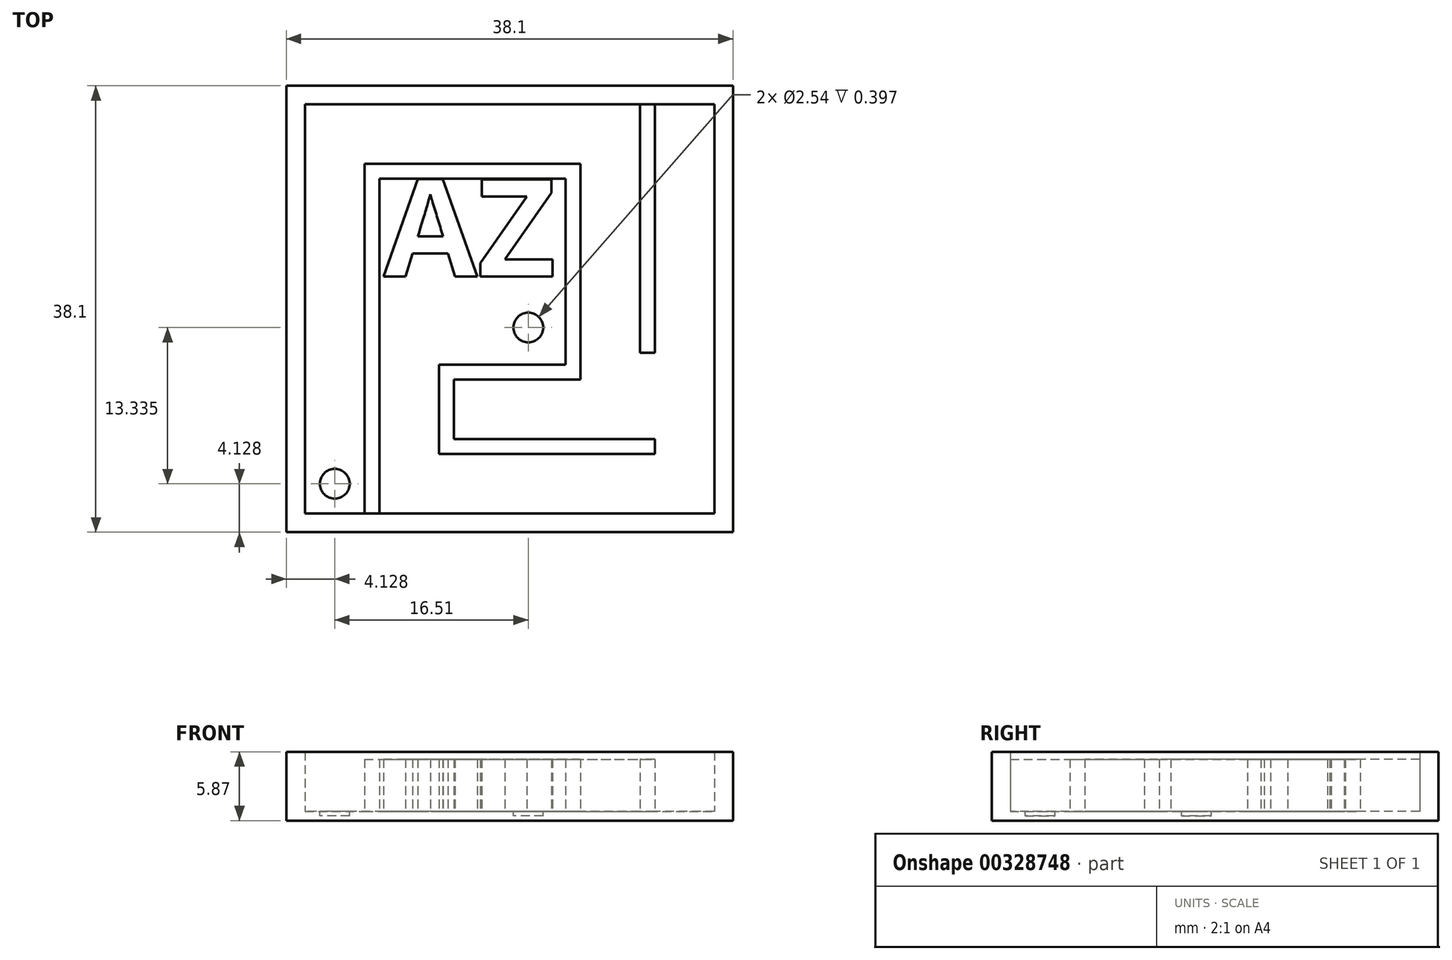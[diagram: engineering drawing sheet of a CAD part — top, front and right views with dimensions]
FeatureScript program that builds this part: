
annotation { "Feature Type Name" : "Feature", "Feature Type Description" : "" }
export const myFeature = defineFeature(function(context is Context, id is Id, definition is map)
    precondition{}
    {
        {
            var Q0;
            Q0=qCreatedBy(makeId("Top.planeOp"),FACE);
            var sketch = newSketch(context, id + "F0", { "sketchPlane" : qUnion([Q0])});
            skLineSegment(sketch, "E0.bottom", {"start": v(19.05, 19.05) * mm, "end": v(-19.05, 19.05) * mm});
            skLineSegment(sketch, "E0.top", {"start": v(19.05, -19.05) * mm, "end": v(-19.05, -19.05) * mm});
            skLineSegment(sketch, "E0.left", {"start": v(19.05, 19.05) * mm, "end": v(19.05, -19.05) * mm});
            skLineSegment(sketch, "E0.right", {"start": v(-19.05, 19.05) * mm, "end": v(-19.05, -19.05) * mm});
            skSolve(sketch);
        }
        {
            var Q0;
            Q0 = qSketchRegion(id + "F0", true);
            extrude(context, id + "F1", {"entities" : qUnion([Q0]), "depth" : 0.8 * mm});
        }
        {
            var Q0;
            Q0=makeQuery(id+"F1.opExtrude","CAP_FACE",FACE,{"disambiguationData":[OSD([sQuery(id+"F0.wireOp",EDGE,"E0.bottom"),sQuery(id+"F0.wireOp",EDGE,"E0.top"),sQuery(id+"F0.wireOp",EDGE,"E0.left"),sQuery(id+"F0.wireOp",EDGE,"E0.right")])],"isStart":false});
            var sketch = newSketch(context, id + "F2", { "sketchPlane" : qUnion([Q0])});
            skLineSegment(sketch, "E1.0", {"start": v(-17.46, -17.46) * mm, "end": v(17.46, -17.46) * mm});
            skLineSegment(sketch, "E1.1", {"start": v(-17.46, 17.46) * mm, "end": v(-17.46, -17.46) * mm});
            skLineSegment(sketch, "E1.2", {"start": v(17.46, 17.46) * mm, "end": v(-17.46, 17.46) * mm});
            skLineSegment(sketch, "E1.3", {"start": v(17.46, -17.46) * mm, "end": v(17.46, 17.46) * mm});
            skSolve(sketch);
        }
        {
            var Q0;
            Q0=makeQuery(id+"F2.imprint","IMPRINT",FACE,{"disambiguationData":[TD([[makeQuery(id+"F2.imprint","IMPRINT",EDGE,{"derivedFrom":sQuery(id+"F2.wireOp",EDGE,"E1.0")}),-1.0]])]});
            extrude(context, id + "F3", {"entities" : qUnion([Q0]), "operationType" : NewBodyOperationType.ADD, "depth" : 5.08 * mm});
        }
        {
            var Q0;
            Q0=makeQuery(id+"F1.opExtrude","CAP_FACE",FACE,{"disambiguationData":[OSD([sQuery(id+"F0.wireOp",EDGE,"E0.bottom"),sQuery(id+"F0.wireOp",EDGE,"E0.top"),sQuery(id+"F0.wireOp",EDGE,"E0.left"),sQuery(id+"F0.wireOp",EDGE,"E0.right")])],"isStart":false});
            var sketch = newSketch(context, id + "F4", { "sketchPlane" : qUnion([Q0])});
            skLineSegment(sketch, "E2.bottom", {"start": v(-12.38, -17.46) * mm, "end": v(-11.11, -17.46) * mm});
            skLineSegment(sketch, "E2.top", {"start": v(-12.38, 12.38) * mm, "end": v(-11.11, 12.38) * mm});
            skLineSegment(sketch, "E2.left", {"start": v(-12.38, -17.46) * mm, "end": v(-12.38, 12.38) * mm});
            skLineSegment(sketch, "E2.right", {"start": v(-11.11, -17.46) * mm, "end": v(-11.11, 11.11) * mm});
            skLineSegment(sketch, "E3.bottom", {"start": v(-11.11, 12.38) * mm, "end": v(6.03, 12.38) * mm});
            skLineSegment(sketch, "E3.top", {"start": v(-11.11, 11.11) * mm, "end": v(4.76, 11.11) * mm});
            skLineSegment(sketch, "E3.right", {"start": v(6.03, 12.38) * mm, "end": v(6.03, 11.11) * mm});
            skLineSegment(sketch, "E4.bottom", {"start": v(12.38, 17.46) * mm, "end": v(11.11, 17.46) * mm});
            skLineSegment(sketch, "E4.top", {"start": v(12.38, -3.75) * mm, "end": v(11.11, -3.75) * mm});
            skLineSegment(sketch, "E4.left", {"start": v(12.38, 17.46) * mm, "end": v(12.38, -3.75) * mm});
            skLineSegment(sketch, "E4.right", {"start": v(11.11, 17.46) * mm, "end": v(11.11, -3.75) * mm});
            skLineSegment(sketch, "E5.top", {"start": v(6.03, -6.03) * mm, "end": v(4.76, -6.03) * mm});
            skLineSegment(sketch, "E5.left", {"start": v(6.03, 11.11) * mm, "end": v(6.03, -6.03) * mm});
            skLineSegment(sketch, "E5.right", {"start": v(4.76, 11.11) * mm, "end": v(4.76, -4.76) * mm});
            skLineSegment(sketch, "E6.bottom", {"start": v(4.76, -6.03) * mm, "end": v(-4.76, -6.03) * mm});
            skLineSegment(sketch, "E6.top", {"start": v(4.76, -4.76) * mm, "end": v(-4.76, -4.76) * mm});
            skLineSegment(sketch, "E6.right", {"start": v(-6.03, -6.03) * mm, "end": v(-6.03, -4.76) * mm});
            skLineSegment(sketch, "E7.top", {"start": v(-6.03, -12.38) * mm, "end": v(-4.76, -12.38) * mm});
            skLineSegment(sketch, "E7.left", {"start": v(-6.03, -6.03) * mm, "end": v(-6.03, -12.38) * mm});
            skLineSegment(sketch, "E7.right", {"start": v(-4.76, -6.03) * mm, "end": v(-4.76, -11.11) * mm});
            skLineSegment(sketch, "E8.bottom", {"start": v(-4.76, -12.38) * mm, "end": v(12.38, -12.38) * mm});
            skLineSegment(sketch, "E8.top", {"start": v(-4.76, -11.11) * mm, "end": v(12.38, -11.11) * mm});
            skLineSegment(sketch, "E8.right", {"start": v(12.38, -12.38) * mm, "end": v(12.38, -11.11) * mm});
            skCircle(sketch, "E9", {"center": v(1.59, -1.59) * mm, "radius": 1.27 * mm});
            skCircle(sketch, "E10", {"center": v(-14.92, -14.92) * mm, "radius": 1.27 * mm});
            skLineSegment(sketch, "E11", {"start": v(-4.76, -4.76) * mm, "end": v(-6.03, -4.76) * mm});
            skText(sketch, "E12", { "text": "AZ", "fontName": "OpenSans-Bold.ttf"});
            const initialGuessF4  = {"E12": [-0.01076, 0.00277, 1, 0, 0.00834]};
            skSetInitialGuess(sketch, initialGuessF4);
            skSolve(sketch);
        }
        {
            var Q0;
            Q0=makeQuery(id+"F4.imprint","IMPRINT",FACE,{"disambiguationData":[TD([[makeQuery(id+"F4.imprint","IMPRINT",EDGE,{"derivedFrom":sQuery(id+"F4.wireOp",EDGE,"E2.bottom")}),1.0]])]});
            var Q1;
            Q1=makeQuery(id+"F4.imprint","IMPRINT",FACE,{"disambiguationData":[TD([[makeQuery(id+"F4.imprint","IMPRINT",EDGE,{"derivedFrom":sQuery(id+"F4.wireOp",EDGE,"E4.bottom")}),1.0]])]});
            var Q2;
            Q2=makeQuery(id+"F4.imprint","IMPRINT",FACE,{"disambiguationData":[TD([[makeQuery(id+"F4.imprint","IMPRINT",EDGE,{"derivedFrom":sQuery(id+"F4.wireOp",EDGE,"E12.sketch_text.stroke-0")}),-1.0]])]});
            var Q3;
            Q3=makeQuery(id+"F4.imprint","IMPRINT",FACE,{"disambiguationData":[TD([[makeQuery(id+"F4.imprint","IMPRINT",EDGE,{"derivedFrom":sQuery(id+"F4.wireOp",EDGE,"E12.sketch_text.stroke-13")}),-1.0]])]});
            extrude(context, id + "F5", {"entities" : qUnion([Q0, Q1, Q2, Q3]), "operationType" : NewBodyOperationType.ADD, "depth" : 4.44 * mm});
        }
        {
            var Q0;
            Q0=makeQuery(id+"F4.imprint","IMPRINT",FACE,{"disambiguationData":[TD([[makeQuery(id+"F4.imprint","IMPRINT",EDGE,{"derivedFrom":sQuery(id+"F4.wireOp",EDGE,"E9")}),1.0]])]});
            var Q1;
            Q1=makeQuery(id+"F4.imprint","IMPRINT",FACE,{"disambiguationData":[TD([[makeQuery(id+"F4.imprint","IMPRINT",EDGE,{"derivedFrom":sQuery(id+"F4.wireOp",EDGE,"E10")}),1.0]])]});
            extrude(context, id + "F6", {"entities" : qUnion([Q0, Q1]), "operationType" : NewBodyOperationType.REMOVE, "oppositeDirection" : true, "depth" : 0.4 * mm});
        }
    });
